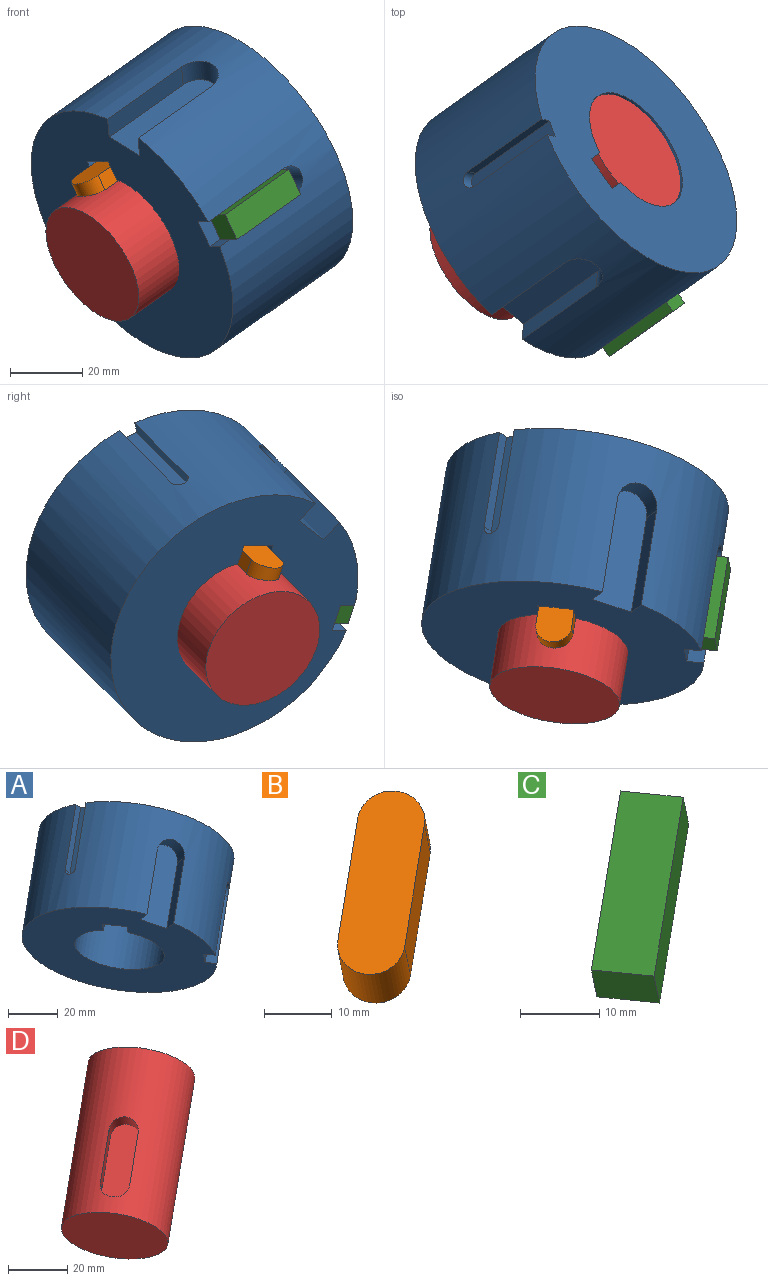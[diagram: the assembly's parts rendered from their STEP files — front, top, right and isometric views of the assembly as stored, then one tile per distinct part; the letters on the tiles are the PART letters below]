
ASSEMBLY  parts=4 mates=3
PART A: 19 faces, bbox 89.1x92x92 mm
  f0: cylinder r=39.53mm len=91.96mm, axis (0.71,0.5,0.5), area 10846.1mm2, adj f1,f2,f8,f9,f10,f12,f13,f14
  f1: plane 68.46x68.46mm, normal (-0.71,-0.5,-0.5), area 3693.2mm2, adj f0,f3,f4,f5,f6,f7,f8,f9
  f2: plane 68.46x68.46mm, normal (0.71,0.5,0.5), area 3797.4mm2, adj f0,f3,f4,f5,f6,f11,f12,f13
  f3: cylinder r=18.21mm len=58.98mm, axis (0.71,0.5,0.5), area 4900mm2, adj f1,f2,f5,f6
  f4: plane 39.01x31.67mm, normal (0.41,0.29,-0.87), area 470mm2, adj f1,f2,f5,f6
  f5: plane 35.56x28.44mm, normal (0.58,-0.82,0), area 267.9mm2, adj f1,f2,f3,f4
  f6: plane 35.56x28.44mm, normal (-0.58,0.82,0), area 267.9mm2, adj f1,f2,f3,f4
  f7: plane 26.11x22.46mm, normal (0.58,-0.82,0), area 265.1mm2, adj f1,f8,f9,f10
  f8: plane 23.98x18.92mm, normal (0.41,0.29,-0.87), area 143.9mm2, adj f0,f1,f7,f10
  f9: plane 23.98x18.92mm, normal (-0.41,-0.29,0.87), area 143.9mm2, adj f0,f1,f7,f10
  f10: cylinder r=4mm len=7.79mm, axis (-0.58,0.82,0), area 61.6mm2, adj f0,f7,f8,f9
  f11: plane 23.16x19.1mm, normal (-0.64,0.16,0.75), area 154.8mm2, adj f2,f12,f13,f14
  f12: plane 22.7x17.07mm, normal (-0.3,0.85,-0.43), area 99.2mm2, adj f0,f2,f11,f14
  f13: plane 22.7x17.07mm, normal (0.3,-0.85,0.43), area 99.2mm2, adj f0,f2,f11,f14
  f14: cylinder r=2.5mm len=5.36mm, axis (0.64,-0.16,-0.75), area 27.2mm2, adj f0,f11,f12,f13
  f15: plane 20.93x19.41mm, normal (0.7,-0.56,-0.43), area 189.7mm2, adj f0,f1,f17,f18
  f16: plane 20.93x19.41mm, normal (-0.7,0.56,0.43), area 189.7mm2, adj f0,f1,f17,f18
  f17: plane 30.72x22.39mm, normal (-0.06,-0.66,0.75), area 404.5mm2, adj f1,f15,f16,f18
  f18: cylinder r=6mm len=12.5mm, axis (0.06,0.66,-0.75), area 127.6mm2, adj f0,f15,f16,f17
PART B: 6 faces, bbox 27.4x22.5x23.7 mm
  f0: plane 23.27x19.57mm, normal (0.41,0.29,-0.87), area 278.5mm2, adj f1,f3,f4,f5
  f1: plane 18.66x18.22mm, normal (-0.58,0.82,0), area 200mm2, adj f0,f2,f4,f5
  f2: plane 23.27x19.57mm, normal (-0.41,-0.29,0.87), area 278.5mm2, adj f1,f3,f4,f5
  f3: plane 18.66x18.22mm, normal (0.58,-0.82,0), area 200mm2, adj f0,f2,f4,f5
  f4: cylinder r=5mm len=11.76mm, axis (0.41,0.29,-0.87), area 157.1mm2, adj f0,f1,f2,f3
  f5: cylinder r=5mm len=11.76mm, axis (-0.41,-0.29,0.87), area 157.1mm2, adj f0,f1,f2,f3
PART C: 6 faces, bbox 25.6x21.3x19.4 mm
  f0: plane 20.94x19.43mm, normal (-0.58,0.82,0), area 200mm2, adj f1,f3,f4,f5
  f1: plane 22.3x19.03mm, normal (-0.41,-0.29,0.87), area 200mm2, adj f0,f2,f4,f5
  f2: plane 20.94x19.43mm, normal (0.58,-0.82,0), area 200mm2, adj f1,f3,f4,f5
  f3: plane 22.3x19.03mm, normal (0.41,0.29,-0.87), area 200mm2, adj f0,f2,f4,f5
  f4: plane 8.84x7.88mm, normal (0.71,0.5,0.5), area 64mm2, adj f0,f1,f2,f3
  f5: plane 8.84x7.88mm, normal (-0.71,-0.5,-0.5), area 64mm2, adj f0,f1,f2,f3
PART D: 8 faces, bbox 69.6x62.5x62.5 mm
  f0: cylinder r=18.21mm len=69.59mm, axis (0.71,0.5,0.5), area 6810mm2, adj f1,f2,f3,f4,f6,f7
  f1: plane 31.53x31.53mm, normal (-0.71,-0.5,-0.5), area 1041.2mm2, adj f0
  f2: plane 31.53x31.53mm, normal (0.71,0.5,0.5), area 1041.2mm2, adj f0
  f3: plane 16.31x14.59mm, normal (0.58,-0.82,0), area 106mm2, adj f0,f5,f6,f7
  f4: plane 16.31x14.59mm, normal (-0.58,0.82,0), area 106mm2, adj f0,f5,f6,f7
  f5: plane 23.27x19.57mm, normal (-0.41,-0.29,0.87), area 278.5mm2, adj f3,f4,f6,f7
  f6: cylinder r=5mm len=10.6mm, axis (-0.41,-0.29,0.87), area 88.8mm2, adj f0,f3,f4,f5
  f7: cylinder r=5mm len=10.6mm, axis (0.41,0.29,-0.87), area 88.8mm2, adj f0,f3,f4,f5
PLACE A t=(33.23,23.5,23.5)mm fixed
PLACE B t=(32.87,23.14,22.71)mm
PLACE C t=(32.59,23.04,23.04)mm
PLACE D t=(32.87,23.14,22.71)mm
MATE fastened D.f5 <-> B.f0  axis (-0.41,-0.29,0.87) through (-1.1,-0.88,12.78)mm
MATE fastened A.f7 <-> C.f0  axis (0.58,-0.82,0) through (31.66,-19.9,8.29)mm
MATE slider D.f0 <-> A.f2  axis (0.71,0.5,0.5) through (32.87,23.14,22.71)mm
